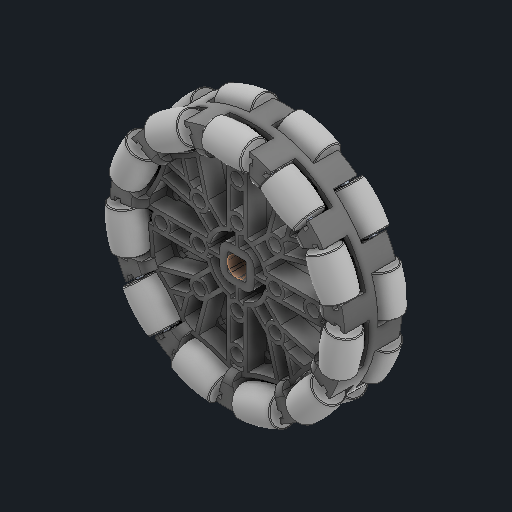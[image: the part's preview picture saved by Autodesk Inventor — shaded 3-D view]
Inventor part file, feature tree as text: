
AUTODESK INVENTOR PART (.ipt)
format: ipt  version: 2024 (Build 280153000, 153)  size: 3,518,464 bytes
history: native  units: in
note: dims shown in document units (in); Inventor stores cm internally (conversion verified against a paired STEP export)
features: other x47, move_body x1, extrude x1
ambient origin geometry x8: Origin, YZ Plane, XZ Plane, XY Plane, X Axis, Y Axis, Z Axis, Center Point
bodies: Solid1 (feature_tree), Solid2 (feature_tree), Solid3 (feature_tree), Solid4 (feature_tree), Solid5 (feature_tree), Solid6 (feature_tree), Solid7 (feature_tree), Solid8 (feature_tree), Solid9 (feature_tree), Solid10 (feature_tree), Solid11 (feature_tree), Solid12 (feature_tree), Solid13 (feature_tree), Solid14 (feature_tree), Solid15 (feature_tree), Solid16 (feature_tree), Solid17 (feature_tree), Solid18 (feature_tree), Solid19 (feature_tree), Solid20 (feature_tree), Solid21 (feature_tree), Solid22 (feature_tree), Solid23 (feature_tree), Solid24 (feature_tree), Solid25 (feature_tree), Solid26 (feature_tree), Solid27 (feature_tree), Solid28 (feature_tree), Solid29 (feature_tree), Solid30 (feature_tree), Solid31 (feature_tree), Solid32 (feature_tree), Solid33 (feature_tree), Solid34 (feature_tree), Solid35 (feature_tree), Solid36 (feature_tree), Solid37 (feature_tree), Solid38 (feature_tree), Solid39 (feature_tree), Solid40 (feature_tree), Solid41 (feature_tree), Solid42 (feature_tree), Solid43 (feature_tree), Solid44 (feature_tree), Solid45 (feature_tree)
feature tree (49):
  other  "3.25 (260mm Travel) Omni-Directional Anti-Static Wheel (276-8026).iam"
  other  "276-8026-001 Web.ipt:1"
  other  "276-8026-002 Web.iam:1::276-3526-001 Web.ipt:1"
  other  "276-8026-002 Web.iam:1::276-8026-003 Web.ipt:1"
  other  "276-8026-002 Web_1.iam:1::276-3526-001 Web.ipt:1"
  other  "276-8026-002 Web_1.iam:1::276-8026-003 Web.ipt:1"
  other  "276-8026-002 Web_2.iam:1::276-3526-001 Web.ipt:1"
  other  "276-8026-002 Web_2.iam:1::276-8026-003 Web.ipt:1"
  other  "276-8026-002 Web_3.iam:1::276-3526-001 Web.ipt:1"
  other  "276-8026-002 Web_3.iam:1::276-8026-003 Web.ipt:1"
  other  "276-8026-002 Web_4.iam:1::276-3526-001 Web.ipt:1"
  other  "276-8026-002 Web_4.iam:1::276-8026-003 Web.ipt:1"
  other  "276-8026-002 Web_5.iam:1::276-3526-001 Web.ipt:1"
  other  "276-8026-002 Web_5.iam:1::276-8026-003 Web.ipt:1"
  other  "276-8026-002 Web_6.iam:1::276-3526-001 Web.ipt:1"
  other  "276-8026-002 Web_6.iam:1::276-8026-003 Web.ipt:1"
  other  "276-8026-002 Web_7.iam:1::276-3526-001 Web.ipt:1"
  other  "276-8026-002 Web_7.iam:1::276-8026-003 Web.ipt:1"
  other  "276-8026-002 Web_8.iam:1::276-3526-001 Web.ipt:1"
  other  "276-8026-002 Web_8.iam:1::276-8026-003 Web.ipt:1"
  other  "276-8026-002 Web_9.iam:1::276-3526-001 Web.ipt:1"
  other  "276-8026-002 Web_9.iam:1::276-8026-003 Web.ipt:1"
  other  "276-8026-002 Web_10.iam:1::276-3526-001 Web.ipt:1"
  other  "276-8026-002 Web_10.iam:1::276-8026-003 Web.ipt:1"
  other  "276-8026-002 Web_11.iam:1::276-3526-001 Web.ipt:1"
  other  "276-8026-002 Web_11.iam:1::276-8026-003 Web.ipt:1"
  other  "276-8026-002 Web_12.iam:1::276-3526-001 Web.ipt:1"
  other  "276-8026-002 Web_12.iam:1::276-8026-003 Web.ipt:1"
  other  "276-8026-002 Web_13.iam:1::276-3526-001 Web.ipt:1"
  other  "276-8026-002 Web_13.iam:1::276-8026-003 Web.ipt:1"
  other  "276-8026-002 Web_14.iam:1::276-3526-001 Web.ipt:1"
  other  "276-8026-002 Web_14.iam:1::276-8026-003 Web.ipt:1"
  other  "276-8026-002 Web_15.iam:1::276-3526-001 Web.ipt:1"
  other  "276-8026-002 Web_15.iam:1::276-8026-003 Web.ipt:1"
  other  "276-8026-002 Web_16.iam:1::276-3526-001 Web.ipt:1"
  other  "276-8026-002 Web_16.iam:1::276-8026-003 Web.ipt:1"
  other  "276-8026-002 Web_17.iam:1::276-3526-001 Web.ipt:1"
  other  "276-8026-002 Web_17.iam:1::276-8026-003 Web.ipt:1"
  other  "276-8026-002 Web_18.iam:1::276-3526-001 Web.ipt:1"
  other  "276-8026-002 Web_18.iam:1::276-8026-003 Web.ipt:1"
  other  "276-8026-002 Web_19.iam:1::276-3526-001 Web.ipt:1"
  other  "276-8026-002 Web_19.iam:1::276-8026-003 Web.ipt:1"
  other  "276-8026-002 Web_20.iam:1::276-3526-001 Web.ipt:1"
  other  "276-8026-002 Web_20.iam:1::276-8026-003 Web.ipt:1"
  other  "276-8026-002 Web_21.iam:1::276-3526-001 Web.ipt:1"
  other  "276-8026-002 Web_21.iam:1::276-8026-003 Web.ipt:1"
  move_body  "Move Body1"
  other  "Srf1"
  extrude  "ExtrusionSrf1"  Depth=0.3937in
